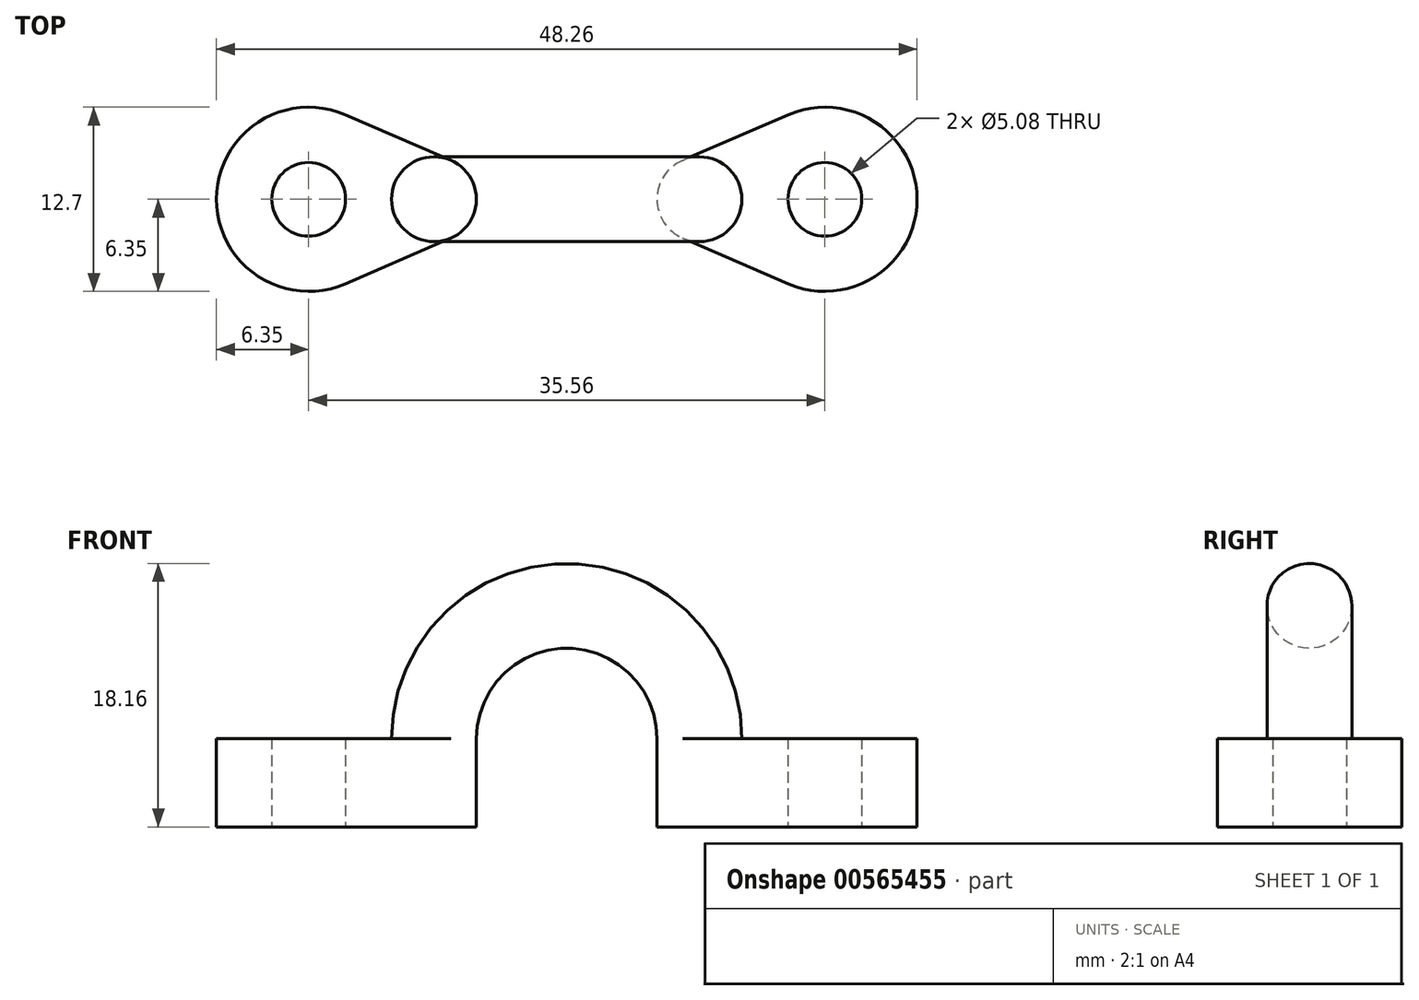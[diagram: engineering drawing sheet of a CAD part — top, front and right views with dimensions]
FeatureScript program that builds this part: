
annotation { "Feature Type Name" : "Feature", "Feature Type Description" : "" }
export const myFeature = defineFeature(function(context is Context, id is Id, definition is map)
    precondition{}
    {
        {
            var Q0;
            Q0=qCreatedBy(makeId("Top.planeOp"),FACE);
            var sketch = newSketch(context, id + "F0", { "sketchPlane" : qUnion([Q0])});
            skCircle(sketch, "E0", {"center": v(9.14, 0) * mm, "radius": 2.92 * mm});
            skSolve(sketch);
        }
        {
            var Q0;
            Q0=qCreatedBy(makeId("Front.planeOp"),FACE);
            var sketch = newSketch(context, id + "F1", { "sketchPlane" : qUnion([Q0])});
            skArc(sketch, "E1", {"start": v(9.14, 0) * mm, "mid": v(0, 9.14) * mm, "end": v(-9.14, 0) * mm});
            skLineSegment(sketch, "E2", {"start": v(-17.65, 0) * mm, "end": v(21.25, 0) * mm, "construction": true});
            skArc(sketch, "E3", {"start": v(6.22, 0) * mm, "mid": v(0, 6.22) * mm, "end": v(-6.22, 0) * mm});
            skSolve(sketch);
        }
        {
            var Q0;
            Q0=qCreatedBy(makeId("Top.planeOp"),FACE);
            cPlane(context, id + "F2", {"entities" : qUnion([Q0]), "cplaneType" : CPlaneType.OFFSET, "offset" : 6.1 * mm, "width" : 152.4 * mm, "height" : 152.4 * mm});
        }
        {
            var Q0;
            Q0=qCreatedBy(id+"F2.planeOp",FACE);
            var sketch = newSketch(context, id + "F3", { "sketchPlane" : qUnion([Q0])});
            skCircle(sketch, "E4", {"center": v(9.14, 0) * mm, "radius": 2.92 * mm});
            skSolve(sketch);
        }
        {
            var Q0;
            Q0=makeQuery(id+"F0.imprint","IMPRINT",FACE,{"disambiguationData":[TD([[makeQuery(id+"F0.imprint","IMPRINT",EDGE,{"derivedFrom":sQuery(id+"F0.wireOp",EDGE,"E0")}),1.0]])]});
            var Q1;
            Q1=makeQuery(id+"F3.imprint","IMPRINT",FACE,{"disambiguationData":[TD([[makeQuery(id+"F3.imprint","IMPRINT",EDGE,{"derivedFrom":sQuery(id+"F3.wireOp",EDGE,"E4")}),1.0]])]});
            loft(context, id + "F4", {"sheetProfilesArray" : [{ "sheetProfileEntities" : qUnion([Q0]) }, { "sheetProfileEntities" : qUnion([Q1]) }]});
        }
        {
            var Q0;
            Q0=qCreatedBy(makeId("Front.planeOp"),FACE);
            var sketch = newSketch(context, id + "F5", { "sketchPlane" : qUnion([Q0])});
            skArc(sketch, "E5", {"start": v(9.14, 6.1) * mm, "mid": v(0, 15.24) * mm, "end": v(-9.14, 6.1) * mm});
            skLineSegment(sketch, "E6", {"start": v(-17.65, 6.1) * mm, "end": v(21.25, 6.1) * mm, "construction": true});
            skArc(sketch, "E7", {"start": v(6.22, 6.1) * mm, "mid": v(0, 12.32) * mm, "end": v(-6.22, 6.1) * mm});
            skSolve(sketch);
        }
        {
            var Q0;
            Q0=makeQuery(id+"F4.opLoft","CAP_FACE",FACE,{"disambiguationData":[OSD([makeQuery(id+"F3.imprint","IMPRINT",FACE,{"disambiguationData":[TD([[makeQuery(id+"F3.imprint","IMPRINT",EDGE,{"derivedFrom":sQuery(id+"F3.wireOp",EDGE,"E4")}),1.0]])]})])],"isStart":true});
            var Q1;
            Q1=sQuery(id+"F5.wireOp",EDGE,"E5");
            sweep(context, id + "F6", {"profiles" : qUnion([Q0]), "path" : qUnion([Q1])});
        }
        {
            var Q0;
            Q0=makeQuery(id+"F4.opLoft","SWEPT_BODY",BODY,{"disambiguationData":[OSD([makeQuery(id+"F0.imprint","IMPRINT",FACE,{"disambiguationData":[TD([[makeQuery(id+"F0.imprint","IMPRINT",EDGE,{"derivedFrom":sQuery(id+"F0.wireOp",EDGE,"E0")}),1.0]])]}),makeQuery(id+"F3.imprint","IMPRINT",FACE,{"disambiguationData":[TD([[makeQuery(id+"F3.imprint","IMPRINT",EDGE,{"derivedFrom":sQuery(id+"F3.wireOp",EDGE,"E4")}),1.0]])]})])]});
            var Q1;
            Q1=qCreatedBy(makeId("Right.planeOp"),FACE);
            mirror(context, id + "F7", {"operationType" : NewBodyOperationType.ADD, "entities" : qUnion([Q0]), "mirrorPlane" : qUnion([Q1])});
        }
        {
            var Q0;
            Q0=qCreatedBy(makeId("Top.planeOp"),FACE);
            var sketch = newSketch(context, id + "F8", { "sketchPlane" : qUnion([Q0])});
            skCircle(sketch, "E8", {"center": v(17.78, 0) * mm, "radius": 2.54 * mm});
            skArc(sketch, "E9", {"start": v(15.26, -5.83) * mm, "mid": v(24.13, 0) * mm, "end": v(15.26, 5.83) * mm});
            skArc(sketch, "E10", {"start": v(7.98, 2.68) * mm, "mid": v(6.22, 0) * mm, "end": v(7.98, -2.68) * mm});
            skLineSegment(sketch, "E11", {"start": v(7.98, 2.68) * mm, "end": v(15.26, 5.83) * mm});
            skLineSegment(sketch, "E12", {"start": v(15.26, -5.83) * mm, "end": v(7.98, -2.68) * mm});
            skPoint(sketch, "E13", {"position": v(24.13, 0) * mm});
            skSolve(sketch);
        }
        {
            var Q0;
            Q0=makeQuery(id+"F8.imprint","IMPRINT",FACE,{"disambiguationData":[TD([[makeQuery(id+"F8.imprint","IMPRINT",EDGE,{"derivedFrom":sQuery(id+"F8.wireOp",EDGE,"E8")}),-1.0]])]});
            extrude(context, id + "F9", {"entities" : qUnion([Q0]), "depth" : 6.1 * mm, "offsetDistance" : 25.4 * mm});
        }
        {
            var Q0;
            Q0=makeQuery(id+"F9.opExtrude","SWEPT_BODY",BODY,{"disambiguationData":[OSD([sQuery(id+"F8.wireOp",EDGE,"E8"),sQuery(id+"F8.wireOp",EDGE,"E9"),sQuery(id+"F8.wireOp",EDGE,"E10"),sQuery(id+"F8.wireOp",EDGE,"E11"),sQuery(id+"F8.wireOp",EDGE,"E12")])]});
            var Q1;
            Q1=qCreatedBy(makeId("Right.planeOp"),FACE);
            mirror(context, id + "F10", {"operationType" : NewBodyOperationType.ADD, "entities" : qUnion([Q0]), "mirrorPlane" : qUnion([Q1])});
        }
    });
